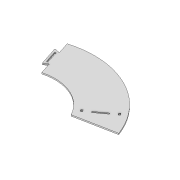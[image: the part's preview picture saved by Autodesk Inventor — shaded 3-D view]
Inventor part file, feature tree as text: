
AUTODESK INVENTOR PART (.ipt)
format: ipt  version: 2020 (Build 240168000, 168)  size: 245,760 bytes
history: native  units: mm
features: extrude x1, sketch x1
ambient origin geometry x8: Origin, YZ Plane, XZ Plane, XY Plane, X Axis, Y Axis, Z Axis, Center Point
bodies: Solid1 (feature_tree)
feature tree (2):
  extrude  "Extrusion1"  Depth=1.75mm
  sketch  "Sketch1"  dims[d0=504.787567mm d1=944.787567mm d2=50.0mm d4=360.0deg d6=7.5mm d7=7.5mm d9=68.5mm d10=7.5mm d11=7.5mm d12=3.5mm d13=3.5mm d17=50.0mm d19=360.0deg d21=4.363323mm d25=10.0mm d26=10.0mm d27=1.75mm d28=30.0mm d30=25.132741mm d32=7.0mm d33=0.0mm d34=0.0mm d35=8.0mm d36=1.75mm d38=50.0mm d40=50.0mm d42=30.0mm d43=8.0mm d44=1.75mm d45=50.0mm d47=360.0deg]
